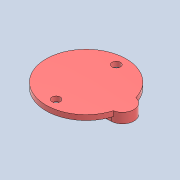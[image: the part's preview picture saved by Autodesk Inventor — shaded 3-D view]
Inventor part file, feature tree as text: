
AUTODESK INVENTOR PART (.ipt)
format: ipt  version: 2022 (Build 260153000, 153)  size: 154,624 bytes
history: native  units: in
note: dims shown in document units (in); Inventor stores cm internally (conversion verified against a paired STEP export)
features: extrude x2, sketch x2, projected_geometry x2, plane x1
ambient origin geometry x8: Origin, YZ Plane, XZ Plane, XY Plane, X Axis, Y Axis, Z Axis, Center Point
bodies: Solid1 (feature_tree)
feature tree (7):
  extrude  "Extrusion1"  Depth=0.125in TaperAngle=0.0deg
  extrude  "Extrusion2"  Depth=0.188in
  plane  "Work Plane1"
  sketch  "Sketch1"  dims[d0=0.2953in d2=0.125in d3=0.0in]
  sketch  "Sketch3"  dims[d4=4.0in d5=4.0in d6=0.125in d7=3.0in d10=0.5357in d12=0.5357in d13=0.8478in d14=0.8478in d15=1.75in d16=2.0in d17=0.208in d18=1.5in d19=0.125in d20=0.0in d25=0.1969in d26=0.9055in d27=0.188in]
  projected_geometry  "Projected Loop1"
  projected_geometry  "Projected Loop2"
